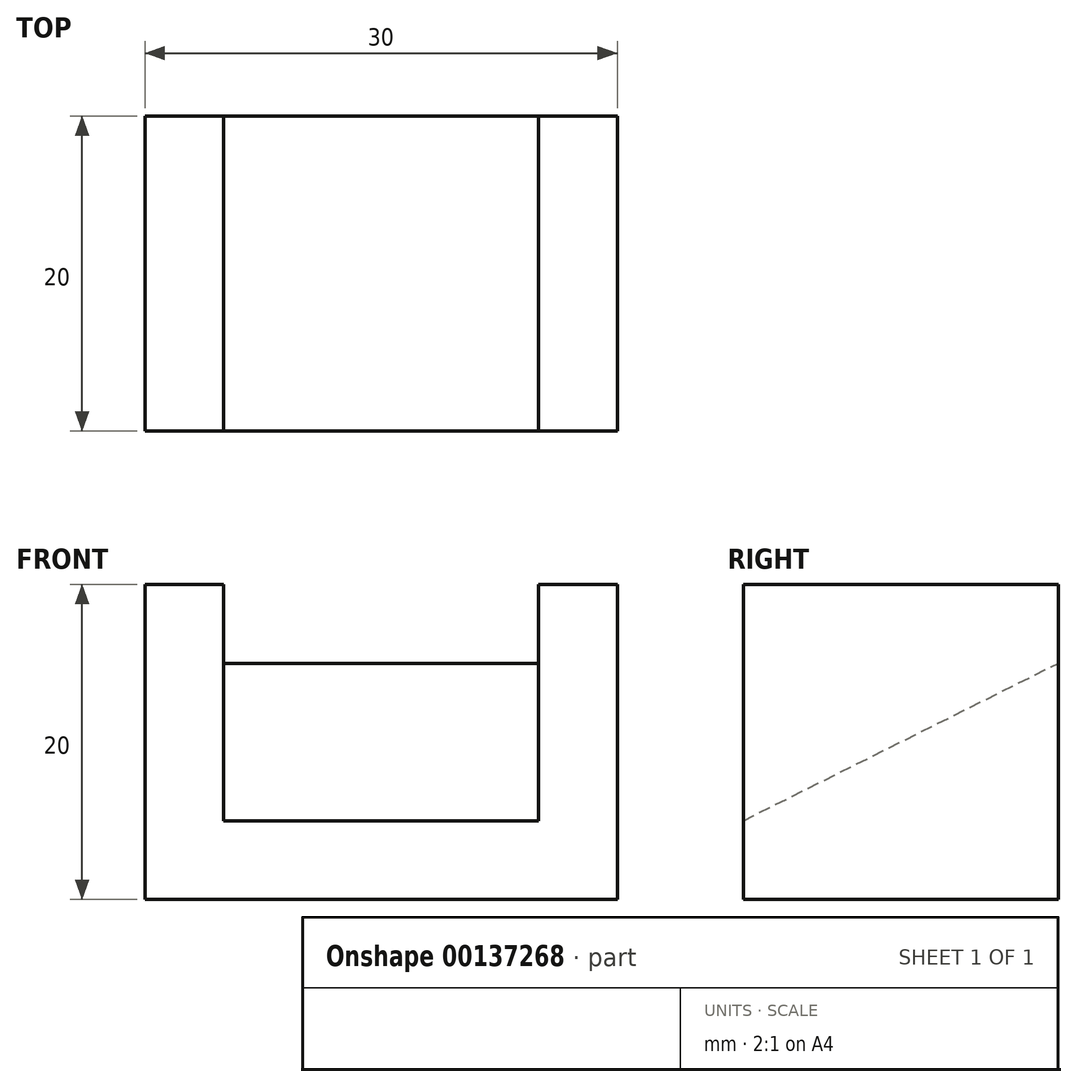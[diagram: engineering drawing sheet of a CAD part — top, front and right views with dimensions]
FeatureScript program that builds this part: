
annotation { "Feature Type Name" : "Feature", "Feature Type Description" : "" }
export const myFeature = defineFeature(function(context is Context, id is Id, definition is map)
    precondition{}
    {
        {
            var Q0;
            Q0=qCreatedBy(makeId("Front.planeOp"),FACE);
            var sketch = newSketch(context, id + "F0", { "sketchPlane" : qUnion([Q0])});
            skLineSegment(sketch, "E0.bottom", {"start": v(0, 0) * mm, "end": v(30, 0) * mm});
            skLineSegment(sketch, "E0.top", {"start": v(0, 20) * mm, "end": v(30, 20) * mm});
            skLineSegment(sketch, "E0.left", {"start": v(0, 0) * mm, "end": v(0, 20) * mm});
            skLineSegment(sketch, "E0.right", {"start": v(30, 0) * mm, "end": v(30, 20) * mm});
            skLineSegment(sketch, "E1", {"start": v(5, 20) * mm, "end": v(5, 5) * mm});
            skLineSegment(sketch, "E2", {"start": v(5, 5) * mm, "end": v(25, 5) * mm});
            skLineSegment(sketch, "E3", {"start": v(25, 5) * mm, "end": v(25, 20) * mm});
            skSolve(sketch);
        }
        {
            var Q0;
            Q0=makeQuery(id+"F0.imprint","IMPRINT",FACE,{"disambiguationData":[TD([[makeQuery(id+"F0.imprint","IMPRINT",EDGE,{"derivedFrom":sQuery(id+"F0.wireOp",EDGE,"E0.bottom")}),1.0]])]});
            extrude(context, id + "F1", {"entities" : qUnion([Q0]), "depth" : 20 * mm});
        }
        {
            var Q0;
            Q0=makeQuery(id+"F1.opExtrude","SWEPT_FACE",FACE,{"disambiguationData":[OSD([sQuery(id+"F0.wireOp",EDGE,"E1")])]});
            var sketch = newSketch(context, id + "F2", { "sketchPlane" : qUnion([Q0])});
            skLineSegment(sketch, "E4.0", {"start": v(-20, 5) * mm, "end": v(0, 5) * mm});
            skLineSegment(sketch, "E5.0", {"start": v(0, 20) * mm, "end": v(0, 5) * mm});
            skLineSegment(sketch, "E6", {"start": v(0, 15) * mm, "end": v(-20, 5) * mm});
            skSolve(sketch);
        }
        {
            var Q0;
            {var subQ0=sQuery(id+"F2.wireOp",EDGE,"E4.0");Q0=makeQuery(id+"F2.imprint","IMPRINT",FACE,{"disambiguationData":[TD([[makeQuery(id+"F2.imprint","IMPRINT",EDGE,{"derivedFrom":subQ0}),1.0]])]});}
            extrude(context, id + "F3", {"entities" : qUnion([Q0]), "operationType" : NewBodyOperationType.ADD, "endBound" : BoundingType.UP_TO_NEXT, "depth" : 25 * mm});
        }
    });
